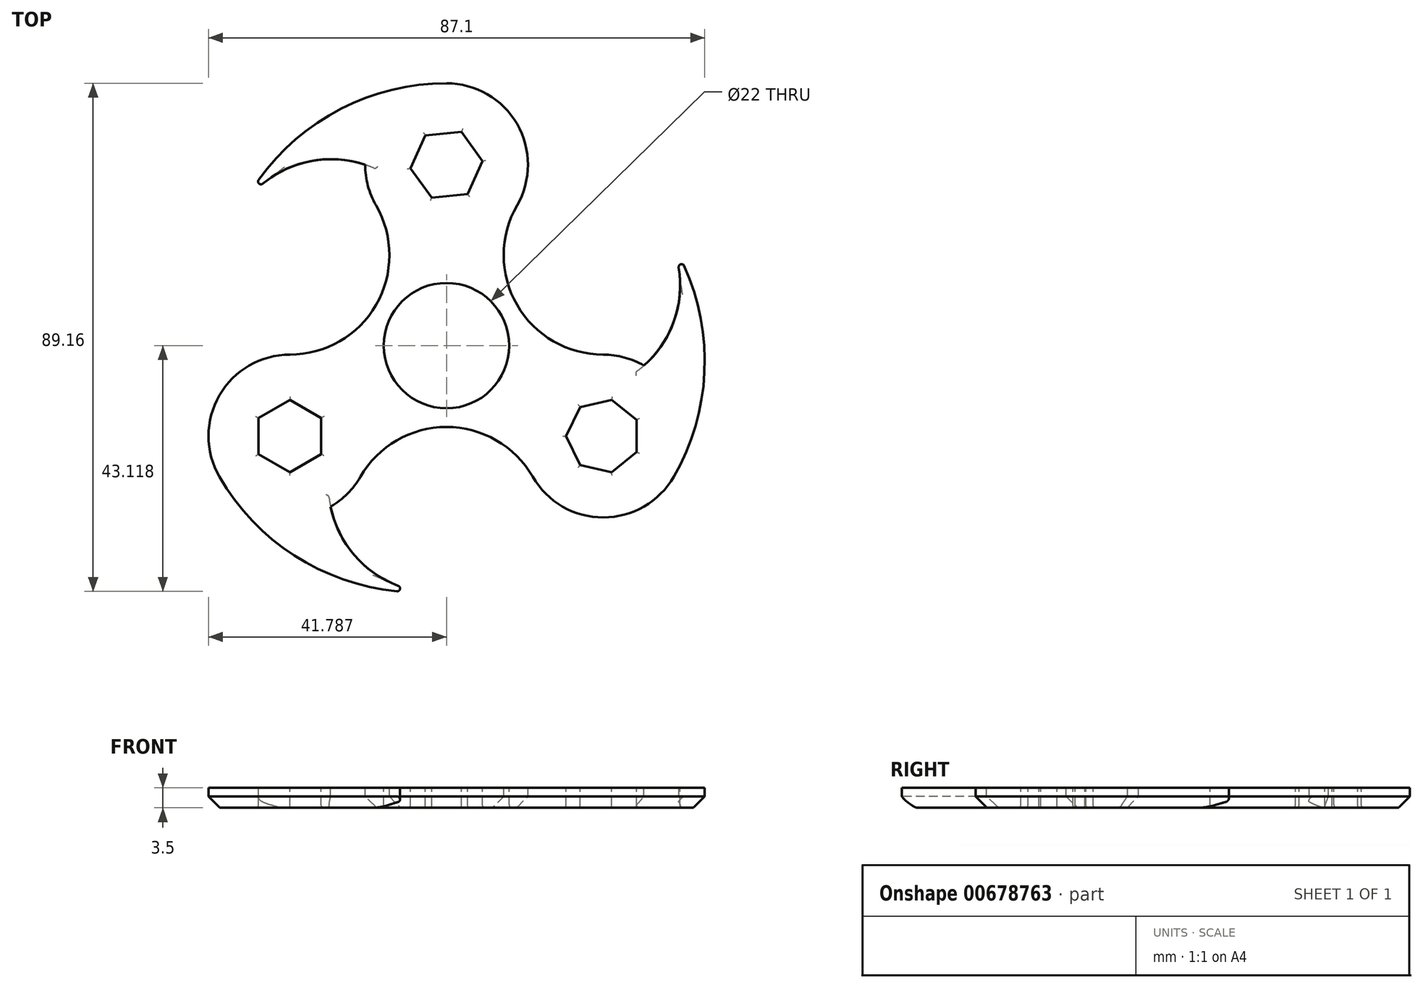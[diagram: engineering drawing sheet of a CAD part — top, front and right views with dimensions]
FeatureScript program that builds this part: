
annotation { "Feature Type Name" : "Feature", "Feature Type Description" : "" }
export const myFeature = defineFeature(function(context is Context, id is Id, definition is map)
    precondition{}
    {
        {
            var Q0;
            Q0=qCreatedBy(makeId("Top.planeOp"),FACE);
            var sketch = newSketch(context, id + "F0", { "sketchPlane" : qUnion([Q0])});
            skArc(sketch, "E0", {"start": v(-15.3, 32.27) * mm, "mid": v(-14.81, 28.57) * mm, "end": v(-13.39, 25.12) * mm});
            skCircle(sketch, "E1", {"center": v(-1.01, 0.52) * mm, "radius": 11 * mm});
            skArc(sketch, "E2.1.1", {"start": v(-28.5, -1.07) * mm, "mid": v(-40.88, -8.21) * mm, "end": v(-40.88, -22.5) * mm});
            skArc(sketch, "E2.2.1", {"start": v(14.11, -22.5) * mm, "mid": v(26.48, -29.64) * mm, "end": v(38.86, -22.5) * mm});
            skArc(sketch, "E3", {"start": v(-28.5, -1.07) * mm, "mid": v(-13.39, 7.66) * mm, "end": v(-13.39, 25.12) * mm});
            skArc(sketch, "E4.1.0", {"start": v(14.11, -22.5) * mm, "mid": v(-1.01, -13.77) * mm, "end": v(-16.14, -22.5) * mm});
            skArc(sketch, "E4.2.0", {"start": v(11.36, 25.12) * mm, "mid": v(11.36, 7.66) * mm, "end": v(26.48, -1.07) * mm});
            skArc(sketch, "E5", {"start": v(-1.01, 46.56) * mm, "mid": v(-21.87, 40.79) * mm, "end": v(-36.8, 25.12) * mm});
            skArc(sketch, "E6", {"start": v(-15.3, 32.27) * mm, "mid": v(-27.24, 32.28) * mm, "end": v(-36.8, 25.12) * mm});
            skPoint(sketch, "E7.center", {"position": v(-2.83, -1.15) * mm});
            skPoint(sketch, "E8.center", {"position": v(0.36, 21.83) * mm});
            skCircle(sketch, "E9.cCircle", {"center": v(26.48, -15.36) * mm, "radius": 5.87 * mm, "construction": true});
            skLineSegment(sketch, "E9.0", {"start": v(32.35, -12.53) * mm, "end": v(32.35, -18.18) * mm});
            skLineSegment(sketch, "E9.1", {"start": v(32.35, -18.18) * mm, "end": v(27.93, -21.7) * mm});
            skLineSegment(sketch, "E9.2", {"start": v(27.93, -21.7) * mm, "end": v(22.42, -20.45) * mm});
            skLineSegment(sketch, "E9.3", {"start": v(22.42, -20.45) * mm, "end": v(19.97, -15.36) * mm});
            skLineSegment(sketch, "E9.4", {"start": v(19.97, -15.36) * mm, "end": v(22.42, -10.26) * mm});
            skLineSegment(sketch, "E9.5", {"start": v(22.42, -10.26) * mm, "end": v(27.93, -9) * mm});
            skLineSegment(sketch, "E9.6", {"start": v(27.93, -9) * mm, "end": v(32.35, -12.53) * mm});
            skPoint(sketch, "E9.0.midPoint", {"position": v(32.35, -15.36) * mm});
            skCircle(sketch, "E10.cCircle", {"center": v(-28.5, -15.36) * mm, "radius": 5.5 * mm, "construction": true});
            skLineSegment(sketch, "E10.0", {"start": v(-34, -18.53) * mm, "end": v(-34, -12.18) * mm});
            skLineSegment(sketch, "E10.1", {"start": v(-34, -12.18) * mm, "end": v(-28.5, -9) * mm});
            skLineSegment(sketch, "E10.2", {"start": v(-28.5, -9) * mm, "end": v(-23, -12.18) * mm});
            skLineSegment(sketch, "E10.3", {"start": v(-23, -12.18) * mm, "end": v(-23, -18.53) * mm});
            skLineSegment(sketch, "E10.4", {"start": v(-23, -18.53) * mm, "end": v(-28.5, -21.7) * mm});
            skLineSegment(sketch, "E10.5", {"start": v(-28.5, -21.7) * mm, "end": v(-34, -18.53) * mm});
            skPoint(sketch, "E10.0.midPoint", {"position": v(-34, -15.36) * mm});
            skCircle(sketch, "E11.cCircle", {"center": v(-1.01, 32.27) * mm, "radius": 5.5 * mm, "construction": true});
            skLineSegment(sketch, "E11.0", {"start": v(2.7, 27.12) * mm, "end": v(-3.62, 26.48) * mm});
            skLineSegment(sketch, "E11.1", {"start": v(-3.62, 26.48) * mm, "end": v(-7.33, 31.63) * mm});
            skLineSegment(sketch, "E11.2", {"start": v(-7.33, 31.63) * mm, "end": v(-4.73, 37.42) * mm});
            skLineSegment(sketch, "E11.3", {"start": v(-4.73, 37.42) * mm, "end": v(1.59, 38.06) * mm});
            skLineSegment(sketch, "E11.4", {"start": v(1.59, 38.06) * mm, "end": v(5.3, 32.91) * mm});
            skLineSegment(sketch, "E11.5", {"start": v(5.3, 32.91) * mm, "end": v(2.7, 27.12) * mm});
            skPoint(sketch, "E11.0.midPoint", {"position": v(-0.46, 26.8) * mm});
            skArc(sketch, "E12.trimOffspring", {"start": v(-5.17, 28.63) * mm, "mid": v(-5.15, 28.62) * mm, "end": v(-5.13, 28.62) * mm});
            skPoint(sketch, "E13.orphan", {"position": v(-8.6, -43.7) * mm});
            skPoint(sketch, "E7.2.0.start.orphan", {"position": v(32.35, -7.06) * mm});
            skArc(sketch, "E14.1.0", {"start": v(-40.88, -22.5) * mm, "mid": v(-25.46, -37.68) * mm, "end": v(-4.43, -42.78) * mm});
            skArc(sketch, "E14.1.1", {"start": v(-21.37, -27.73) * mm, "mid": v(-15.4, -38.07) * mm, "end": v(-4.43, -42.78) * mm});
            skArc(sketch, "E14.2.0", {"start": v(38.86, -22.5) * mm, "mid": v(44.3, -1.55) * mm, "end": v(38.2, 19.2) * mm});
            skArc(sketch, "E14.2.1", {"start": v(33.63, -2.98) * mm, "mid": v(39.6, 7.35) * mm, "end": v(38.2, 19.2) * mm});
            skArc(sketch, "E15.trimOffspring", {"start": v(33.63, -2.98) * mm, "mid": v(30.18, -1.56) * mm, "end": v(26.48, -1.07) * mm});
            skArc(sketch, "E16.trimOffspring", {"start": v(-21.37, -27.73) * mm, "mid": v(-18.4, -25.46) * mm, "end": v(-16.14, -22.5) * mm});
            skArc(sketch, "E17.trimOffspring", {"start": v(11.36, 25.12) * mm, "mid": v(11.36, 39.41) * mm, "end": v(-1.01, 46.56) * mm});
            skSolve(sketch);
        }
        {
            var Q0;
            Q0=makeQuery(id+"F0.imprint","IMPRINT",FACE,{"disambiguationData":[TD([[makeQuery(id+"F0.imprint","IMPRINT",EDGE,{"derivedFrom":sQuery(id+"F0.wireOp",EDGE,"E0")}),1.0]])]});
            extrude(context, id + "F1", {"entities" : qUnion([Q0]), "oppositeDirection" : true, "depth" : 3.5 * mm, "offsetDistance" : 25 * mm});
        }
        {
            var Q0;
            Q0=makeQuery(id+"F1.opExtrude","CAP_EDGE",EDGE,{"disambiguationData":[OSD([sQuery(id+"F0.wireOp",EDGE,"E14.1.0")])],"isStart":false});
            var Q1;
            Q1=makeQuery(id+"F1.opExtrude","CAP_EDGE",EDGE,{"disambiguationData":[OSD([sQuery(id+"F0.wireOp",EDGE,"E4.2.0")])],"isStart":false});
            var Q2;
            Q2=makeQuery(id+"F1.opExtrude","CAP_EDGE",EDGE,{"disambiguationData":[OSD([sQuery(id+"F0.wireOp",EDGE,"E2.2.1")])],"isStart":false});
            chamfer(context, id + "F2", {"entities" : qUnion([Q0, Q1, Q2]), "width" : 2 * mm, "tangentPropagation" : true});
        }
        {
            var Q0;
            Q0=makeQuery(id+"F1.opExtrude","CAP_FACE",FACE,{"disambiguationData":[OSD([sQuery(id+"F0.wireOp",EDGE,"E0"),sQuery(id+"F0.wireOp",EDGE,"E1"),sQuery(id+"F0.wireOp",EDGE,"E2.1.1"),sQuery(id+"F0.wireOp",EDGE,"E2.2.1"),sQuery(id+"F0.wireOp",EDGE,"E3"),sQuery(id+"F0.wireOp",EDGE,"E4.1.0"),sQuery(id+"F0.wireOp",EDGE,"E4.2.0"),sQuery(id+"F0.wireOp",EDGE,"E5"),sQuery(id+"F0.wireOp",EDGE,"E6"),sQuery(id+"F0.wireOp",EDGE,"E9.0"),sQuery(id+"F0.wireOp",EDGE,"E9.1"),sQuery(id+"F0.wireOp",EDGE,"E9.2"),sQuery(id+"F0.wireOp",EDGE,"E9.3"),sQuery(id+"F0.wireOp",EDGE,"E9.4"),sQuery(id+"F0.wireOp",EDGE,"E9.5"),sQuery(id+"F0.wireOp",EDGE,"E9.6"),sQuery(id+"F0.wireOp",EDGE,"E10.0"),sQuery(id+"F0.wireOp",EDGE,"E10.1"),sQuery(id+"F0.wireOp",EDGE,"E10.2"),sQuery(id+"F0.wireOp",EDGE,"E10.3"),sQuery(id+"F0.wireOp",EDGE,"E10.4"),sQuery(id+"F0.wireOp",EDGE,"E10.5"),sQuery(id+"F0.wireOp",EDGE,"E11.0"),sQuery(id+"F0.wireOp",EDGE,"E11.1"),sQuery(id+"F0.wireOp",EDGE,"E11.2"),sQuery(id+"F0.wireOp",EDGE,"E11.3"),sQuery(id+"F0.wireOp",EDGE,"E11.4"),sQuery(id+"F0.wireOp",EDGE,"E11.5"),sQuery(id+"F0.wireOp",EDGE,"E14.1.0"),sQuery(id+"F0.wireOp",EDGE,"E14.1.1"),sQuery(id+"F0.wireOp",EDGE,"E14.2.0"),sQuery(id+"F0.wireOp",EDGE,"E14.2.1"),sQuery(id+"F0.wireOp",EDGE,"E15.trimOffspring"),sQuery(id+"F0.wireOp",EDGE,"E16.trimOffspring"),sQuery(id+"F0.wireOp",EDGE,"E17.trimOffspring")])],"isStart":false});
            var Q1;
            Q1=makeQuery(id+"F1.opExtrude","SWEPT_EDGE",EDGE,{"disambiguationData":[OSD([sQuery(id+"F0.wireOp",EDGE,"E14.2.0"),sQuery(id+"F0.wireOp",EDGE,"E14.2.1")])]});
            var Q2;
            Q2=makeQuery(id+"F1.opExtrude","SWEPT_EDGE",EDGE,{"disambiguationData":[OSD([sQuery(id+"F0.wireOp",EDGE,"E5"),sQuery(id+"F0.wireOp",EDGE,"E6")])]});
            var Q3;
            Q3=makeQuery(id+"F1.opExtrude","SWEPT_EDGE",EDGE,{"disambiguationData":[OSD([sQuery(id+"F0.wireOp",EDGE,"E14.1.0"),sQuery(id+"F0.wireOp",EDGE,"E14.1.1")])]});
            fillet(context, id + "F3", {"entities" : qUnion([Q0, Q1, Q2, Q3]), "radius" : 0.5 * mm, "tangentPropagation" : true, "allowEdgeOverflow" : false});
        }
    });
